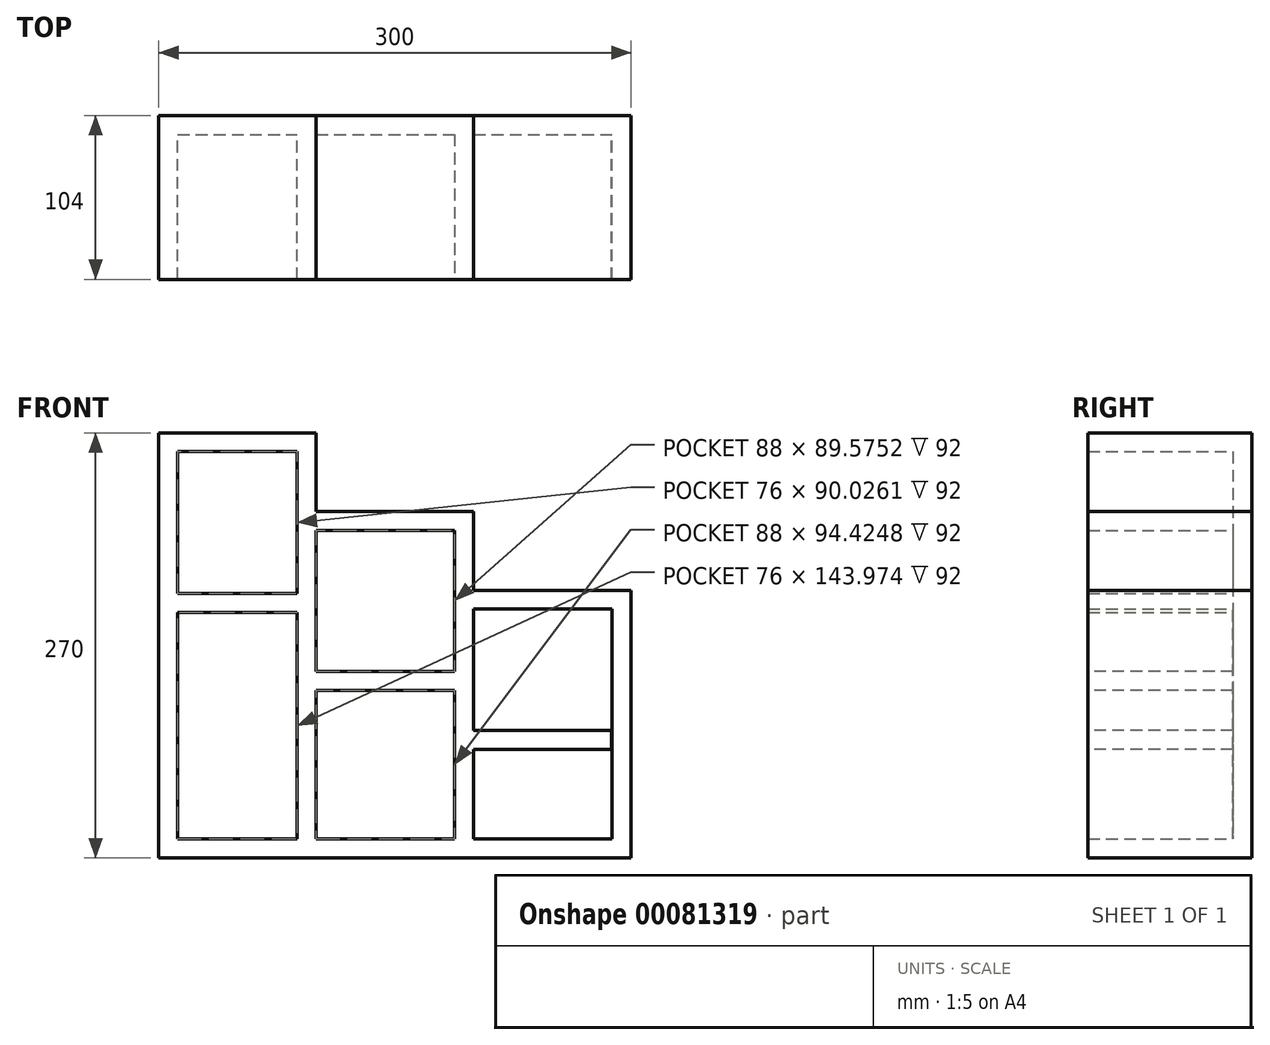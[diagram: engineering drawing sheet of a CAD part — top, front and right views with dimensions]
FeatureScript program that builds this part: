
annotation { "Feature Type Name" : "Feature", "Feature Type Description" : "" }
export const myFeature = defineFeature(function(context is Context, id is Id, definition is map)
    precondition{}
    {
        {
            var Q0;
            Q0=qCreatedBy(makeId("Front.planeOp"),FACE);
            var sketch = newSketch(context, id + "F0", { "sketchPlane" : qUnion([Q0])});
            skLineSegment(sketch, "E0", {"start": v(-189.35, -170) * mm, "end": v(110.65, -170) * mm});
            skLineSegment(sketch, "E1", {"start": v(-189.35, -170) * mm, "end": v(-189.35, 100) * mm});
            skLineSegment(sketch, "E2", {"start": v(-89.35, 100) * mm, "end": v(-89.35, 50) * mm});
            skLineSegment(sketch, "E3", {"start": v(10.65, 50) * mm, "end": v(10.65, 0) * mm});
            skLineSegment(sketch, "E4", {"start": v(110.65, -170) * mm, "end": v(110.65, 0) * mm});
            skLineSegment(sketch, "E5", {"start": v(-189.35, 100) * mm, "end": v(-89.35, 100) * mm});
            skLineSegment(sketch, "E6", {"start": v(-89.35, 50) * mm, "end": v(10.65, 50) * mm});
            skLineSegment(sketch, "E7", {"start": v(10.65, 0) * mm, "end": v(110.65, 0) * mm});
            skSolve(sketch);
        }
        {
            var Q0;
            Q0=makeQuery(id+"F0.imprint","IMPRINT",FACE,{"disambiguationData":[TD([[makeQuery(id+"F0.imprint","IMPRINT",EDGE,{"derivedFrom":sQuery(id+"F0.wireOp",EDGE,"E0")}),1.0]])]});
            extrude(context, id + "F1", {"entities" : qUnion([Q0]), "depth" : 104 * mm});
        }
        {
            var Q0;
            Q0=makeQuery(id+"F1.opExtrude","CAP_FACE",FACE,{"disambiguationData":[OSD([sQuery(id+"F0.wireOp",EDGE,"E0"),sQuery(id+"F0.wireOp",EDGE,"E1"),sQuery(id+"F0.wireOp",EDGE,"E2"),sQuery(id+"F0.wireOp",EDGE,"E3"),sQuery(id+"F0.wireOp",EDGE,"E4"),sQuery(id+"F0.wireOp",EDGE,"E5"),sQuery(id+"F0.wireOp",EDGE,"E6"),sQuery(id+"F0.wireOp",EDGE,"E7")])],"isStart":false});
            shell(context, id + "F2", {"entities" : qUnion([Q0]), "thickness" : 12 * mm});
        }
        {
            var Q0;
            Q0=makeQuery(id+"F2.opShell","OFFSET_FACE",FACE,{"disambiguationData":[OSD([sQuery(id+"F0.wireOp",EDGE,"E0"),sQuery(id+"F0.wireOp",EDGE,"E1"),sQuery(id+"F0.wireOp",EDGE,"E2"),sQuery(id+"F0.wireOp",EDGE,"E3"),sQuery(id+"F0.wireOp",EDGE,"E4"),sQuery(id+"F0.wireOp",EDGE,"E5"),sQuery(id+"F0.wireOp",EDGE,"E6"),sQuery(id+"F0.wireOp",EDGE,"E7")])]});
            var sketch = newSketch(context, id + "F3", { "sketchPlane" : qUnion([Q0])});
            skLineSegment(sketch, "E8.bottom", {"start": v(-101.35, 38) * mm, "end": v(-89.35, 38) * mm});
            skLineSegment(sketch, "E8.top", {"start": v(-101.35, -162) * mm, "end": v(-89.35, -162) * mm});
            skLineSegment(sketch, "E8.left", {"start": v(-101.35, 38) * mm, "end": v(-101.35, -162) * mm});
            skLineSegment(sketch, "E8.right", {"start": v(-89.35, 38) * mm, "end": v(-89.35, -162) * mm});
            skLineSegment(sketch, "E9.bottom", {"start": v(-1.35, -12) * mm, "end": v(10.65, -12) * mm});
            skLineSegment(sketch, "E9.top", {"start": v(-1.35, -162) * mm, "end": v(10.65, -162) * mm});
            skLineSegment(sketch, "E9.left", {"start": v(-1.35, -12) * mm, "end": v(-1.35, -162) * mm});
            skLineSegment(sketch, "E9.right", {"start": v(10.65, -12) * mm, "end": v(10.65, -162) * mm});
            skSolve(sketch);
        }
        {
            var Q0;
            {var subQ0=sQuery(id+"F3.wireOp",EDGE,"E8.bottom");Q0=makeQuery(id+"F3.imprint","IMPRINT",FACE,{"disambiguationData":[TD([[makeQuery(id+"F3.imprint","IMPRINT",EDGE,{"derivedFrom":subQ0}),-1.0]])]});}
            var Q1;
            {var subQ0=sQuery(id+"F3.wireOp",EDGE,"E9.bottom");Q1=makeQuery(id+"F3.imprint","IMPRINT",FACE,{"disambiguationData":[TD([[makeQuery(id+"F3.imprint","IMPRINT",EDGE,{"derivedFrom":subQ0}),-1.0]])]});}
            extrude(context, id + "F4", {"entities" : qUnion([Q0, Q1]), "operationType" : NewBodyOperationType.ADD, "depth" : 92 * mm});
        }
        {
            var Q0;
            {var subQ0=sQuery(id+"F0.wireOp",EDGE,"E5");var subQ1=sQuery(id+"F0.wireOp",EDGE,"E2");var subQ2=sQuery(id+"F0.wireOp",EDGE,"E1");var subQ3=sQuery(id+"F0.wireOp",EDGE,"E0");Q0=makeQuery(id+"F4.boolean.opBoolean","SPLIT",FACE,{"disambiguationData":[TD([makeQuery(id+"F2.opShell","OFFSET_FACE",FACE,{"disambiguationData":[OSD([subQ2])]})])],"derivedFrom":makeQuery(id+"F2.opShell","OFFSET_FACE",FACE,{"disambiguationData":[OSD([subQ3,subQ2,subQ1,sQuery(id+"F0.wireOp",EDGE,"E3"),sQuery(id+"F0.wireOp",EDGE,"E4"),subQ0,sQuery(id+"F0.wireOp",EDGE,"E6"),sQuery(id+"F0.wireOp",EDGE,"E7")])]})});}
            var sketch = newSketch(context, id + "F5", { "sketchPlane" : qUnion([Q0])});
            skLineSegment(sketch, "E10.bottom", {"start": v(-177.35, -2.03) * mm, "end": v(-101.35, -2.03) * mm});
            skLineSegment(sketch, "E10.top", {"start": v(-177.35, -14.03) * mm, "end": v(-101.35, -14.03) * mm});
            skLineSegment(sketch, "E10.left", {"start": v(-177.35, -2.03) * mm, "end": v(-177.35, -14.03) * mm});
            skLineSegment(sketch, "E10.right", {"start": v(-101.35, -2.03) * mm, "end": v(-101.35, -14.03) * mm});
            skLineSegment(sketch, "E11.bottom", {"start": v(-89.89, -51.58) * mm, "end": v(0, -51.58) * mm});
            skLineSegment(sketch, "E11.top", {"start": v(-89.89, -63.58) * mm, "end": v(0, -63.58) * mm});
            skLineSegment(sketch, "E11.left", {"start": v(-89.89, -51.58) * mm, "end": v(-89.89, -63.58) * mm});
            skLineSegment(sketch, "E11.right", {"start": v(0, -51.58) * mm, "end": v(0, -63.58) * mm});
            skLineSegment(sketch, "E12.bottom", {"start": v(10.34, -89.02) * mm, "end": v(98.17, -89.02) * mm});
            skLineSegment(sketch, "E12.top", {"start": v(10.34, -101.02) * mm, "end": v(98.17, -101.02) * mm});
            skLineSegment(sketch, "E12.left", {"start": v(10.34, -89.02) * mm, "end": v(10.34, -101.02) * mm});
            skLineSegment(sketch, "E12.right", {"start": v(98.17, -89.02) * mm, "end": v(98.17, -101.02) * mm});
            skSolve(sketch);
        }
        {
            var Q0;
            Q0=makeQuery(id+"F5.imprint","IMPRINT",FACE,{"disambiguationData":[TD([[makeQuery(id+"F5.imprint","IMPRINT",EDGE,{"derivedFrom":sQuery(id+"F5.wireOp",EDGE,"E10.bottom")}),-1.0]])]});
            var Q1;
            Q1=makeQuery(id+"F5.imprint","IMPRINT",FACE,{"disambiguationData":[TD([[makeQuery(id+"F5.imprint","IMPRINT",EDGE,{"derivedFrom":sQuery(id+"F5.wireOp",EDGE,"E11.bottom")}),-1.0]])]});
            var Q2;
            Q2=makeQuery(id+"F5.imprint","IMPRINT",FACE,{"disambiguationData":[TD([[makeQuery(id+"F5.imprint","IMPRINT",EDGE,{"derivedFrom":sQuery(id+"F5.wireOp",EDGE,"E12.bottom")}),-1.0]])]});
            extrude(context, id + "F6", {"entities" : qUnion([Q0, Q1, Q2]), "operationType" : NewBodyOperationType.ADD, "depth" : 92 * mm});
        }
    });
